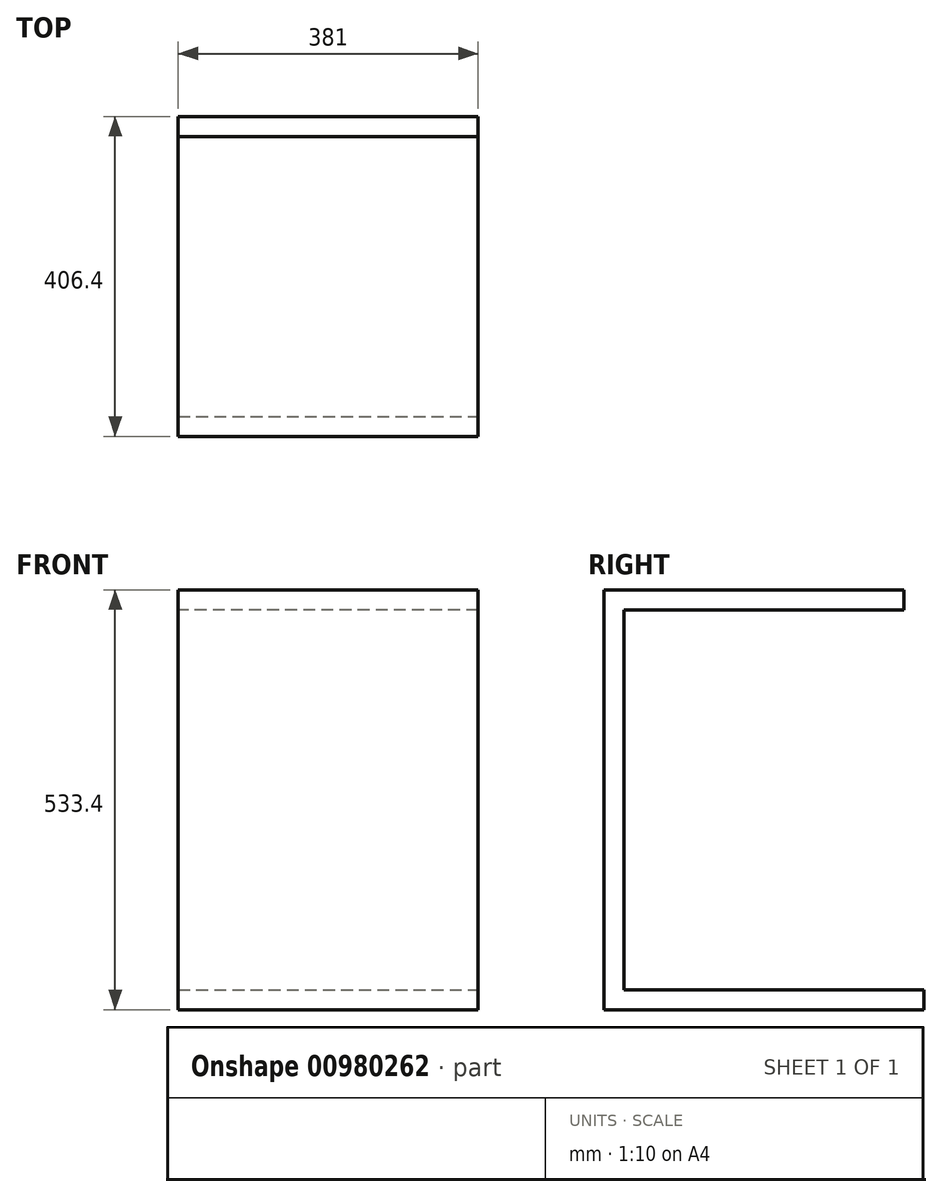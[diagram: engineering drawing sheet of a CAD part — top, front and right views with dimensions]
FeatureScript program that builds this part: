
annotation { "Feature Type Name" : "Feature", "Feature Type Description" : "" }
export const myFeature = defineFeature(function(context is Context, id is Id, definition is map)
    precondition{}
    {
        {
            var Q0;
            Q0=qCreatedBy(makeId("Top.planeOp"),FACE);
            var sketch = newSketch(context, id + "F0", { "sketchPlane" : qUnion([Q0])});
            skLineSegment(sketch, "E0.bottom", {"start": v(0, 0) * mm, "end": v(381, 0) * mm});
            skLineSegment(sketch, "E0.top", {"start": v(0, 381) * mm, "end": v(381, 381) * mm});
            skLineSegment(sketch, "E0.left", {"start": v(0, 0) * mm, "end": v(0, 381) * mm});
            skLineSegment(sketch, "E0.right", {"start": v(381, 0) * mm, "end": v(381, 381) * mm});
            skSolve(sketch);
        }
        {
            var Q0;
            Q0 = qSketchRegion(id + "F0", true);
            extrude(context, id + "F1", {"entities" : qUnion([Q0]), "depth" : 25.4 * mm, "offsetDistance" : 25.4 * mm});
        }
        {
            var Q0;
            Q0=qCreatedBy(makeId("Right.planeOp"),FACE);
            var sketch = newSketch(context, id + "F2", { "sketchPlane" : qUnion([Q0])});
            skLineSegment(sketch, "E1.bottom", {"start": v(0, 0) * mm, "end": v(-25.4, 0) * mm});
            skLineSegment(sketch, "E1.top", {"start": v(0, 508) * mm, "end": v(-25.4, 508) * mm});
            skLineSegment(sketch, "E1.left", {"start": v(0, 0) * mm, "end": v(0, 508) * mm});
            skLineSegment(sketch, "E1.right", {"start": v(-25.4, 0) * mm, "end": v(-25.4, 508) * mm});
            skSolve(sketch);
        }
        {
            var Q0;
            Q0 = qSketchRegion(id + "F2", true);
            extrude(context, id + "F3", {"entities" : qUnion([Q0]), "operationType" : NewBodyOperationType.ADD, "depth" : 381 * mm, "offsetDistance" : 25.4 * mm});
        }
        {
            var Q0;
            Q0=makeQuery(id+"F3.opExtrude","SWEPT_FACE",FACE,{"disambiguationData":[OSD([sQuery(id+"F2.wireOp",EDGE,"E1.top")])]});
            var sketch = newSketch(context, id + "F4", { "sketchPlane" : qUnion([Q0])});
            skLineSegment(sketch, "E2.bottom", {"start": v(381, -25.4) * mm, "end": v(0, -25.4) * mm});
            skLineSegment(sketch, "E2.top", {"start": v(381, 355.6) * mm, "end": v(0, 355.6) * mm});
            skLineSegment(sketch, "E2.left", {"start": v(381, -25.4) * mm, "end": v(381, 355.6) * mm});
            skLineSegment(sketch, "E2.right", {"start": v(0, -25.4) * mm, "end": v(0, 355.6) * mm});
            skSolve(sketch);
        }
        {
            var Q0;
            {var subQ0=sQuery(id+"F4.wireOp",EDGE,"E2.top");Q0=makeQuery(id+"F4.imprint","IMPRINT",FACE,{"disambiguationData":[TD([[makeQuery(id+"F4.imprint","IMPRINT",EDGE,{"derivedFrom":subQ0}),1.0]])]});}
            var Q1;
            {var subQ0=sQuery(id+"F4.wireOp",EDGE,"E2.bottom");Q1=makeQuery(id+"F4.imprint","IMPRINT",FACE,{"disambiguationData":[TD([[makeQuery(id+"F4.imprint","IMPRINT",EDGE,{"derivedFrom":subQ0}),-1.0]])]});}
            extrude(context, id + "F5", {"entities" : qUnion([Q0, Q1]), "operationType" : NewBodyOperationType.ADD, "depth" : 25.4 * mm, "offsetDistance" : 25.4 * mm});
        }
    });
